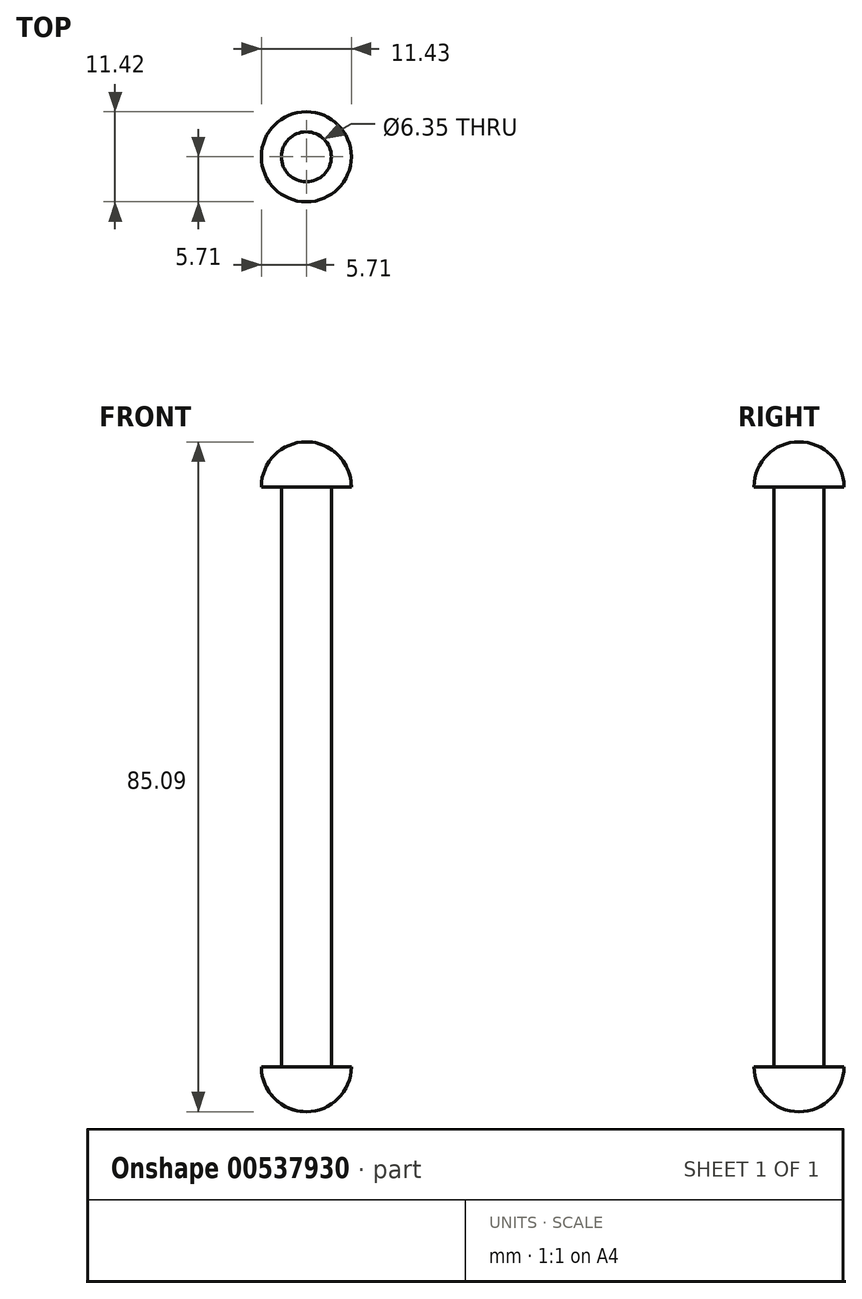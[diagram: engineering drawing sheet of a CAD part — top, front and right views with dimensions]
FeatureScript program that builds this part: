
annotation { "Feature Type Name" : "Feature", "Feature Type Description" : "" }
export const myFeature = defineFeature(function(context is Context, id is Id, definition is map)
    precondition{}
    {
        {
            var Q0;
            Q0=qCreatedBy(makeId("Front.planeOp"),FACE);
            var sketch = newSketch(context, id + "F0", { "sketchPlane" : qUnion([Q0])});
            skLineSegment(sketch, "E0", {"start": v(0, 0) * mm, "end": v(0, 85.1) * mm, "construction": true});
            skPoint(sketch, "E1.visualSharp", {"position": v(5.77, 0) * mm});
            skLineSegment(sketch, "E2.0", {"start": v(3.18, 5.72) * mm, "end": v(3.18, 79.38) * mm});
            skLineSegment(sketch, "E3", {"start": v(0, 85.1) * mm, "end": v(0, 85.1) * mm});
            skLineSegment(sketch, "E4", {"start": v(0, 0) * mm, "end": v(0, 0) * mm});
            skLineSegment(sketch, "E5.0", {"start": v(3.18, 5.72) * mm, "end": v(5.72, 5.72) * mm});
            skPoint(sketch, "E6.visualSharp", {"position": v(5.71, 85.1) * mm});
            skArc(sketch, "E6.filletArc", {"start": v(5.72, 79.38) * mm, "mid": v(4.04, 83.42) * mm, "end": v(0, 85.1) * mm});
            skArc(sketch, "E7.filletArc", {"start": v(0, 0) * mm, "mid": v(4.04, 1.67) * mm, "end": v(5.72, 5.71) * mm});
            skLineSegment(sketch, "E8", {"start": v(3.18, 79.38) * mm, "end": v(5.72, 79.38) * mm});
            skSolve(sketch);
        }
        {
            var Q0;
            Q0=sQuery(id+"F0.wireOp",EDGE,"E0");
            var Q1;
            Q1=sQuery(id+"F0.wireOp",EDGE,"E6.filletArc");
            var Q2;
            Q2=sQuery(id+"F0.wireOp",EDGE,"E8");
            var Q3;
            Q3=sQuery(id+"F0.wireOp",EDGE,"E2.0");
            var Q4;
            Q4=sQuery(id+"F0.wireOp",EDGE,"E5.0");
            var Q5;
            Q5=sQuery(id+"F0.wireOp",EDGE,"E7.filletArc");
            var Q6;
            Q6=sQuery(id+"F0.wireOp",EDGE,"E0");
            revolve(context, id + "F1", {"bodyType" : ToolBodyType.SURFACE, "surfaceEntities" : qUnion([Q0, Q1, Q2, Q3, Q4, Q5]), "axis" : qUnion([Q6]), "revolveType" : RevolveType.FULL});
        }
    });
